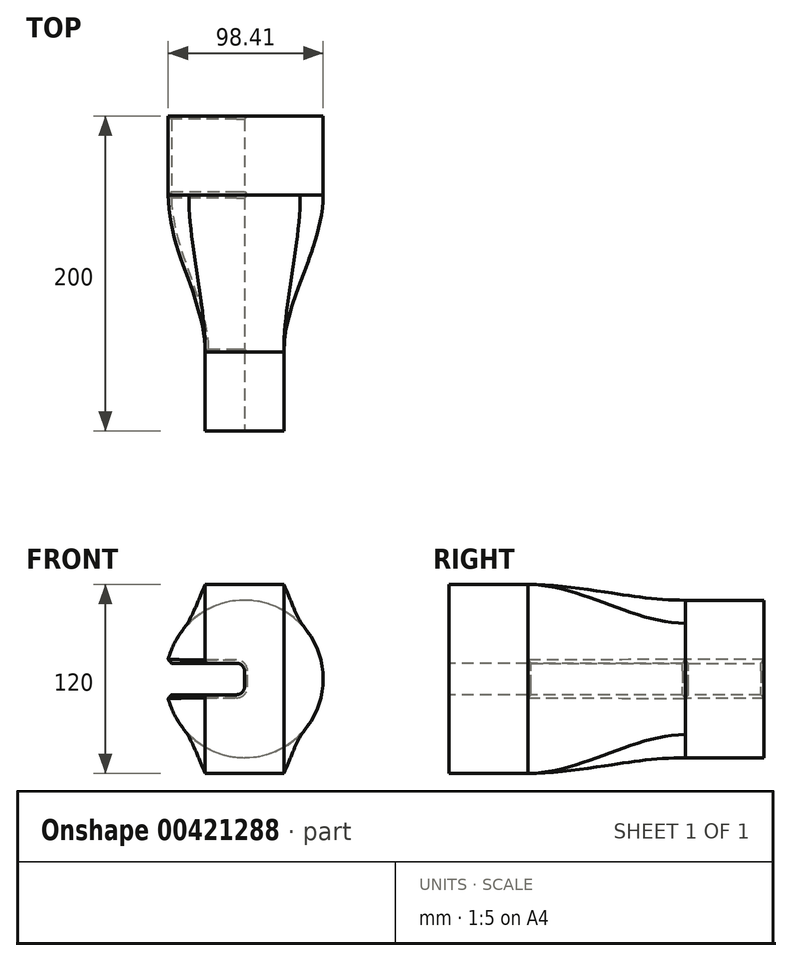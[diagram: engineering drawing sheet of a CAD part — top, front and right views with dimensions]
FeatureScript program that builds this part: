
annotation { "Feature Type Name" : "Feature", "Feature Type Description" : "" }
export const myFeature = defineFeature(function(context is Context, id is Id, definition is map)
    precondition{}
    {
        {
            var Q0;
            Q0=qCreatedBy(makeId("Front.planeOp"),FACE);
            var sketch = newSketch(context, id + "F0", { "sketchPlane" : qUnion([Q0])});
            skCircle(sketch, "E0", {"center": v(0, 0) * mm, "radius": 50 * mm});
            skSolve(sketch);
        }
        {
            var Q0;
            Q0=qCreatedBy(makeId("Front.planeOp"),FACE);
            cPlane(context, id + "F1", {"entities" : qUnion([Q0]), "cplaneType" : CPlaneType.OFFSET, "offset" : 100 * mm, "width" : 150 * mm, "height" : 150 * mm});
        }
        {
            var Q0;
            Q0=qCreatedBy(id+"F1.planeOp",FACE);
            var sketch = newSketch(context, id + "F2", { "sketchPlane" : qUnion([Q0])});
            skLineSegment(sketch, "E1.bottom", {"start": v(25, 60) * mm, "end": v(-25, 60) * mm});
            skLineSegment(sketch, "E1.top", {"start": v(25, -60) * mm, "end": v(-25, -60) * mm});
            skLineSegment(sketch, "E1.left", {"start": v(25, 60) * mm, "end": v(25, -60) * mm});
            skLineSegment(sketch, "E1.right", {"start": v(-25, 60) * mm, "end": v(-25, -60) * mm});
            skPoint(sketch, "E1.middle", {"position": v(0, 0) * mm});
            skSolve(sketch);
        }
        {
            var Q0;
            Q0=makeQuery(id+"F2.imprint","IMPRINT",FACE,{"disambiguationData":[TD([[makeQuery(id+"F2.imprint","IMPRINT",EDGE,{"derivedFrom":sQuery(id+"F2.wireOp",EDGE,"E1.bottom")}),1.0]])]});
            extrude(context, id + "F3", {"entities" : qUnion([Q0]), "depth" : 50 * mm});
        }
        {
            var Q0;
            Q0=makeQuery(id+"F0.imprint","IMPRINT",FACE,{"disambiguationData":[TD([[makeQuery(id+"F0.imprint","IMPRINT",EDGE,{"derivedFrom":sQuery(id+"F0.wireOp",EDGE,"E0")}),1.0]])]});
            extrude(context, id + "F4", {"entities" : qUnion([Q0]), "oppositeDirection" : true, "depth" : 50 * mm});
        }
        {
            var Q0;
            Q0=makeQuery(id+"F4.opExtrude","CAP_FACE",FACE,{"disambiguationData":[OSD([sQuery(id+"F0.wireOp",EDGE,"E0")])],"isStart":true});
            var sketch = newSketch(context, id + "F5", { "sketchPlane" : qUnion([Q0])});
            skArc(sketch, "E2", {"start": v(-35.36, 35.36) * mm, "mid": v(-50, 0) * mm, "end": v(-35.36, -35.36) * mm});
            skArc(sketch, "E3", {"start": v(35.36, 35.36) * mm, "mid": v(0, 50) * mm, "end": v(-35.36, 35.36) * mm});
            skArc(sketch, "E4", {"start": v(35.36, -35.36) * mm, "mid": v(50, 0) * mm, "end": v(35.36, 35.36) * mm});
            skArc(sketch, "E5", {"start": v(-35.36, -35.36) * mm, "mid": v(0, -50) * mm, "end": v(35.36, -35.36) * mm});
            skLineSegment(sketch, "E6", {"start": v(0, 70.4) * mm, "end": v(0, -73.39) * mm, "construction": true});
            skLineSegment(sketch, "E7", {"start": v(-78.44, 0) * mm, "end": v(77.32, 0) * mm, "construction": true});
            skLineSegment(sketch, "E8", {"start": v(0, 0) * mm, "end": v(35.36, 35.36) * mm, "construction": true});
            skSolve(sketch);
        }
        {
            var Q0;
            Q0=makeQuery(id+"F4.opExtrude","CAP_FACE",FACE,{"disambiguationData":[OSD([sQuery(id+"F0.wireOp",EDGE,"E0")])],"isStart":true});
            var Q1;
            Q1=makeQuery(id+"F3.opExtrude","CAP_FACE",FACE,{"disambiguationData":[OSD([sQuery(id+"F2.wireOp",EDGE,"E1.bottom"),sQuery(id+"F2.wireOp",EDGE,"E1.top"),sQuery(id+"F2.wireOp",EDGE,"E1.left"),sQuery(id+"F2.wireOp",EDGE,"E1.right")])],"isStart":true});
            var Q2;
            Q2=makeQuery(id+"F4.opExtrude","CAP_FACE",FACE,{"disambiguationData":[OSD([sQuery(id+"F0.wireOp",EDGE,"E0")])],"isStart":true});
            var Q3;
            Q3=makeQuery(id+"F3.opExtrude","CAP_FACE",FACE,{"disambiguationData":[OSD([sQuery(id+"F2.wireOp",EDGE,"E1.bottom"),sQuery(id+"F2.wireOp",EDGE,"E1.top"),sQuery(id+"F2.wireOp",EDGE,"E1.left"),sQuery(id+"F2.wireOp",EDGE,"E1.right")])],"isStart":true});
            var Q4;
            Q4=sQuery(id+"F2.wireOp",VERTEX,"E1.right.start");
            var Q5;
            Q5=sQuery(id+"F5.wireOp",VERTEX,"E3.end");
            loft(context, id + "F6", {"startCondition" : LoftEndDerivativeType.MATCH_TANGENT, "startMagnitude" : 1, "endCondition" : LoftEndDerivativeType.MATCH_TANGENT, "endMagnitude" : 1, "sheetProfilesArray" : [{ "sheetProfileEntities" : qUnion([Q0]) }, { "sheetProfileEntities" : qUnion([Q1]) }], "wireProfilesArray" : [{ "wireProfileEntities" : qUnion([Q2]) }, { "wireProfileEntities" : qUnion([Q3]) }], "matchConnections" : true, "connections" : [{ "connectionEntities" : qUnion([Q4, Q5]), "connectionEdgeQueries" : qUnion([]), "connectionEdgeParameters" : [] }]});
        }
        {
            var Q0;
            Q0=makeQuery(id+"F3.opExtrude","CAP_FACE",FACE,{"disambiguationData":[OSD([sQuery(id+"F2.wireOp",EDGE,"E1.bottom"),sQuery(id+"F2.wireOp",EDGE,"E1.top"),sQuery(id+"F2.wireOp",EDGE,"E1.left"),sQuery(id+"F2.wireOp",EDGE,"E1.right")])],"isStart":false});
            var sketch = newSketch(context, id + "F7", { "sketchPlane" : qUnion([Q0])});
            skLineSegment(sketch, "E9.bottom", {"start": v(-25, -10) * mm, "end": v(0, -10) * mm});
            skLineSegment(sketch, "E9.top", {"start": v(-25, 10) * mm, "end": v(0, 10) * mm});
            skLineSegment(sketch, "E9.left", {"start": v(-25, -10) * mm, "end": v(-25, 10) * mm});
            skLineSegment(sketch, "E9.right", {"start": v(0, -10) * mm, "end": v(0, 10) * mm});
            skLineSegment(sketch, "E10", {"start": v(15.73, 0) * mm, "end": v(-62.5, 0) * mm, "construction": true});
            skSolve(sketch);
        }
        {
            var Q0;
            Q0=makeQuery(id+"F7.imprint","IMPRINT",FACE,{"disambiguationData":[TD([[makeQuery(id+"F7.imprint","IMPRINT",EDGE,{"derivedFrom":sQuery(id+"F7.wireOp",EDGE,"E9.bottom")}),1.0]])]});
            extrude(context, id + "F8", {"entities" : qUnion([Q0]), "operationType" : NewBodyOperationType.REMOVE, "oppositeDirection" : true, "depth" : 250 * mm});
        }
        {
            var Q0;
            Q0=makeQuery(id+"F8.boolean.opBoolean","COPY",FACE,{"derivedFrom":makeQuery(id+"F8.opExtrude","SWEPT_FACE",FACE,{"disambiguationData":[OSD([sQuery(id+"F7.wireOp",EDGE,"E9.right")])]})});
            extrude(context, id + "F9", {"entities" : qUnion([Q0]), "operationType" : NewBodyOperationType.REMOVE, "depth" : 141 * mm});
        }
        {
            var Q0;
            Q0=makeQuery(id+"F8.boolean.opBoolean","COPY",EDGE,{"derivedFrom":makeQuery(id+"F8.opExtrude","SWEPT_EDGE",EDGE,{"disambiguationData":[OSD([sQuery(id+"F7.wireOp",EDGE,"E9.top"),sQuery(id+"F7.wireOp",EDGE,"E9.right")])]})});
            var Q1;
            Q1=makeQuery(id+"F8.boolean.opBoolean","COPY",EDGE,{"derivedFrom":makeQuery(id+"F8.opExtrude","SWEPT_EDGE",EDGE,{"disambiguationData":[OSD([sQuery(id+"F7.wireOp",EDGE,"E9.bottom"),sQuery(id+"F7.wireOp",EDGE,"E9.right")])]})});
            fillet(context, id + "F10", {"entities" : qUnion([Q0, Q1]), "radius" : 5 * mm, "tangentPropagation" : true, "allowEdgeOverflow" : false});
        }
        {
            var Q0;
            {var subQ0=sQuery(id+"F7.wireOp",EDGE,"E9.bottom");Q0=makeQuery(id+"F9.boolean.opBoolean","MERGE",FACE,{"derivedFrom":[makeQuery(id+"F8.boolean.opBoolean","COPY",FACE,{"derivedFrom":makeQuery(id+"F8.opExtrude","SWEPT_FACE",FACE,{"disambiguationData":[OSD([subQ0])]})}),makeQuery(id+"F9.opExtrude","SWEPT_FACE",FACE,{"disambiguationData":[OSD([subQ0,sQuery(id+"F7.wireOp",EDGE,"E9.right")])]})]});}
            var Q1;
            {var subQ0=sQuery(id+"F7.wireOp",EDGE,"E9.top");Q1=makeQuery(id+"F9.boolean.opBoolean","MERGE",FACE,{"derivedFrom":[makeQuery(id+"F8.boolean.opBoolean","COPY",FACE,{"derivedFrom":makeQuery(id+"F8.opExtrude","SWEPT_FACE",FACE,{"disambiguationData":[OSD([subQ0])]})}),makeQuery(id+"F9.opExtrude","SWEPT_FACE",FACE,{"disambiguationData":[OSD([subQ0,sQuery(id+"F7.wireOp",EDGE,"E9.right")])]})]});}
            chamfer(context, id + "F11", {"entities" : qUnion([Q0, Q1]), "width" : 2 * mm, "tangentPropagation" : true});
        }
        {
            var Q0;
            Q0=makeQuery(id+"F3.opExtrude","CAP_FACE",FACE,{"disambiguationData":[OSD([sQuery(id+"F2.wireOp",EDGE,"E1.bottom"),sQuery(id+"F2.wireOp",EDGE,"E1.top"),sQuery(id+"F2.wireOp",EDGE,"E1.left"),sQuery(id+"F2.wireOp",EDGE,"E1.right")])],"isStart":false});
            var sketch = newSketch(context, id + "F12", { "sketchPlane" : qUnion([Q0])});
            skLineSegment(sketch, "E11", {"start": v(41.4, 0) * mm, "end": v(-63.18, 0) * mm, "construction": true});
            skPoint(sketch, "E11.startSnap0", {"position": v(25, 0) * mm});
            skPoint(sketch, "E11.endSnap0", {"position": v(25, 0) * mm});
            skLineSegment(sketch, "E12", {"start": v(0, 91.62) * mm, "end": v(0, -92) * mm, "construction": true});
            skPoint(sketch, "E12.startSnap0", {"position": v(0, 60) * mm});
            skPoint(sketch, "E12.endSnap0", {"position": v(0, -60) * mm});
            skPoint(sketch, "E13", {"position": v(-15, 45) * mm});
            skLineSegment(sketch, "E14.MirrorCS", {"start": v(0, -91.62) * mm, "end": v(0, 92) * mm, "construction": true});
            skPoint(sketch, "E15.MirrorP", {"position": v(-15, -45) * mm});
            skPoint(sketch, "E16.MirrorP", {"position": v(15, -45) * mm});
            skPoint(sketch, "E17.MirrorP", {"position": v(15, 45) * mm});
            skSolve(sketch);
        }
        {
            var Q0;
            Q0=sQuery(id+"F12.wireOp",VERTEX,"E15.MirrorP");
            var Q1;
            Q1=sQuery(id+"F12.wireOp",VERTEX,"E13");
            var Q2;
            Q2=sQuery(id+"F12.wireOp",VERTEX,"E17.MirrorP");
            var Q3;
            Q3=sQuery(id+"F12.wireOp",VERTEX,"E16.MirrorP");
            var Q4;
            Q4=makeQuery(id+"F4.opExtrude","SWEPT_BODY",BODY,{"disambiguationData":[OSD([sQuery(id+"F0.wireOp",EDGE,"E0")])]});
            hole(context, id + "F13", {"style" : HoleStyle.SIMPLE, "endStyle" : HoleEndStyle.BLIND, "standardTappedOrClearance" : lookupTablePath({ "standard" : "ISO", "engagement" : "75%", "pitch" : "1.5 mm", "size" : "M12", "type" : "Tapped" }), "standardBlindInLast" : lookupTablePath({ "standard" : "ISO", "engagement" : "75%", "pitch" : "1.5 mm", "size" : "M12", "type" : "Tapped" }), "holeDiameter" : 10.5 * mm, "showTappedDepth" : true, "holeDepth" : 16.5 * mm, "isTappedThrough" : true, "tappedDepth" : 12 * mm, "tapClearance" : 3, "locations" : qUnion([Q0, Q1, Q2, Q3]), "scope" : qUnion([Q4]), "majorDiameter" : 12 * mm});
        }
    });
